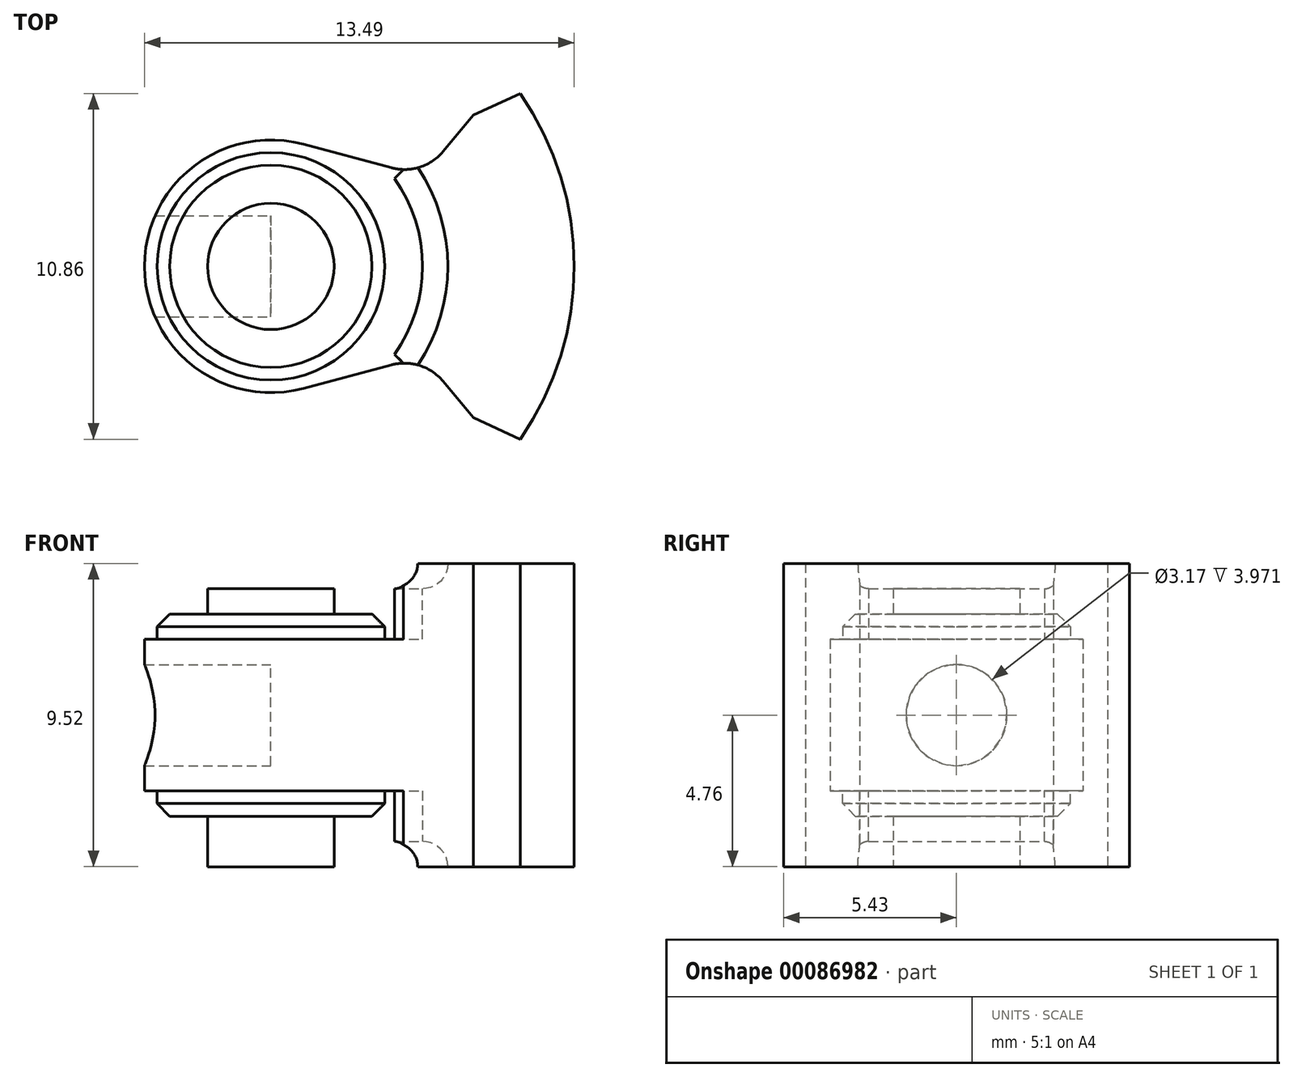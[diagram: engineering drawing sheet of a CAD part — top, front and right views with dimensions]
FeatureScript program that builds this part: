
annotation { "Feature Type Name" : "Feature", "Feature Type Description" : "" }
export const myFeature = defineFeature(function(context is Context, id is Id, definition is map)
    precondition{}
    {
        {
            var Q0;
            Q0=qCreatedBy(makeId("Top.planeOp"),FACE);
            var sketch = newSketch(context, id + "F0", { "sketchPlane" : qUnion([Q0])});
            skCircle(sketch, "E0", {"center": v(0, 0) * mm, "radius": 9.53 * mm, "construction": true});
            skCircle(sketch, "E1", {"center": v(0, 0) * mm, "radius": 7.94 * mm, "construction": true});
            skCircle(sketch, "E2", {"center": v(0, 0) * mm, "radius": 4.76 * mm, "construction": true});
            skCircle(sketch, "E3", {"center": v(0, 0) * mm, "radius": 3.97 * mm, "construction": true});
            skLineSegment(sketch, "E4", {"start": v(0, 0) * mm, "end": v(2.38, 0) * mm, "construction": true});
            skLineSegment(sketch, "E5", {"start": v(2.38, 0) * mm, "end": v(11.06, 10.34) * mm, "construction": true});
            skLineSegment(sketch, "E6", {"start": v(2.38, 0) * mm, "end": v(10.97, -10.23) * mm, "construction": true});
            skLineSegment(sketch, "E7", {"start": v(6.36, 4.75) * mm, "end": v(7.83, 5.43) * mm});
            skLineSegment(sketch, "E8", {"start": v(6.36, -4.75) * mm, "end": v(7.83, -5.43) * mm});
            skLineSegment(sketch, "E9", {"start": v(1.03, -3.83) * mm, "end": v(6.07, -2.48) * mm, "construction": true});
            skLineSegment(sketch, "E10", {"start": v(1.03, 3.83) * mm, "end": v(5.56, 2.62) * mm, "construction": true});
            skArc(sketch, "E11", {"start": v(5.4, -3.6) * mm, "mid": v(4.67, -3.11) * mm, "end": v(3.78, -3.1) * mm});
            skArc(sketch, "E12", {"start": v(3.78, 3.1) * mm, "mid": v(4.67, 3.11) * mm, "end": v(5.4, 3.6) * mm});
            skArc(sketch, "E13", {"start": v(1.03, 3.83) * mm, "mid": v(-2.42, 3.15) * mm, "end": v(-3.97, 0) * mm});
            skLineSegment(sketch, "E14", {"start": v(5.4, 3.6) * mm, "end": v(6.36, 4.75) * mm});
            skLineSegment(sketch, "E15", {"start": v(1.03, 3.83) * mm, "end": v(3.78, 3.1) * mm});
            skLineSegment(sketch, "E16", {"start": v(1.03, -3.83) * mm, "end": v(3.78, -3.1) * mm});
            skLineSegment(sketch, "E17", {"start": v(6.36, -4.75) * mm, "end": v(5.4, -3.6) * mm});
            skArc(sketch, "E18", {"start": v(9.52, 0) * mm, "mid": v(9.1, 2.84) * mm, "end": v(7.83, 5.43) * mm});
            skLineSegment(sketch, "E19", {"start": v(-3.97, 0) * mm, "end": v(9.53, 0) * mm});
            skSolve(sketch);
        }
        {
            var Q0;
            Q0=makeQuery(id+"F0.imprint","IMPRINT",FACE,{"disambiguationData":[TD([[makeQuery(id+"F0.imprint","IMPRINT",EDGE,{"derivedFrom":sQuery(id+"F0.wireOp",EDGE,"E7")}),-1.0]])]});
            extrude(context, id + "F1", {"entities" : qUnion([Q0]), "depth" : 4.76 * mm});
        }
        {
            var Q0;
            Q0=makeQuery(id+"F1.opExtrude","CAP_FACE",FACE,{"disambiguationData":[OSD([sQuery(id+"F0.wireOp",EDGE,"E7"),sQuery(id+"F0.wireOp",EDGE,"E8"),sQuery(id+"F0.wireOp",EDGE,"E11"),sQuery(id+"F0.wireOp",EDGE,"E12"),sQuery(id+"F0.wireOp",EDGE,"E13"),sQuery(id+"F0.wireOp",EDGE,"E14"),sQuery(id+"F0.wireOp",EDGE,"E15"),sQuery(id+"F0.wireOp",EDGE,"E16"),sQuery(id+"F0.wireOp",EDGE,"E17"),sQuery(id+"F0.wireOp",EDGE,"E18")])],"isStart":false});
            var sketch = newSketch(context, id + "F2", { "sketchPlane" : qUnion([Q0])});
            skCircle(sketch, "E20", {"center": v(0, 0) * mm, "radius": 4.76 * mm, "construction": true});
            skCircle(sketch, "E21", {"center": v(0, 0) * mm, "radius": 3.97 * mm, "construction": true});
            skLineSegment(sketch, "E22", {"start": v(1.03, 3.83) * mm, "end": v(3.57, 3.15) * mm});
            skLineSegment(sketch, "E23", {"start": v(1.03, -3.83) * mm, "end": v(3.57, -3.15) * mm});
            skArc(sketch, "E24", {"start": v(3.57, -3.15) * mm, "mid": v(4.76, 0) * mm, "end": v(3.57, 3.15) * mm});
            skArc(sketch, "E25", {"start": v(1.03, 3.83) * mm, "mid": v(-3.97, 0) * mm, "end": v(1.03, -3.83) * mm, "construction": true});
            skSolve(sketch);
        }
        {
            var Q0;
            Q0=makeQuery(id+"F2.imprint","IMPRINT",FACE,{"disambiguationData":[TD([[makeQuery(id+"F2.imprint","IMPRINT",EDGE,{"derivedFrom":sQuery(id+"F2.wireOp",EDGE,"E22")}),-1.0]])]});
            extrude(context, id + "F3", {"entities" : qUnion([Q0]), "operationType" : NewBodyOperationType.REMOVE, "oppositeDirection" : true, "depth" : 2.38 * mm});
        }
        {
            var Q0;
            Q0=qCreatedBy(makeId("Front.planeOp"),FACE);
            var sketch = newSketch(context, id + "F4", { "sketchPlane" : qUnion([Q0])});
            skLineSegment(sketch, "E26", {"start": v(0, 0) * mm, "end": v(0, 4.76) * mm, "construction": true});
            skLineSegment(sketch, "E27", {"start": v(0, 4.76) * mm, "end": v(4.76, 4.76) * mm, "construction": true});
            skCircle(sketch, "E28", {"center": v(4.76, 4.76) * mm, "radius": 0.8 * mm});
            skSolve(sketch);
        }
        {
            var Q0;
            Q0=makeQuery(id+"F1.opExtrude","CAP_FACE",FACE,{"disambiguationData":[OSD([sQuery(id+"F0.wireOp",EDGE,"E7"),sQuery(id+"F0.wireOp",EDGE,"E8"),sQuery(id+"F0.wireOp",EDGE,"E11"),sQuery(id+"F0.wireOp",EDGE,"E12"),sQuery(id+"F0.wireOp",EDGE,"E13"),sQuery(id+"F0.wireOp",EDGE,"E14"),sQuery(id+"F0.wireOp",EDGE,"E15"),sQuery(id+"F0.wireOp",EDGE,"E16"),sQuery(id+"F0.wireOp",EDGE,"E17"),sQuery(id+"F0.wireOp",EDGE,"E18")])],"isStart":false});
            var sketch = newSketch(context, id + "F5", { "sketchPlane" : qUnion([Q0])});
            skArc(sketch, "E29", {"start": v(4.76, 0) * mm, "mid": v(4.45, 1.69) * mm, "end": v(3.57, 3.15) * mm});
            skSolve(sketch);
        }
        {
            var Q0;
            Q0 = qSketchRegion(id + "F4", true);
            var Q1;
            Q1=sQuery(id+"F4.wireOp",EDGE,"E28");
            var Q2;
            Q2=sQuery(id+"F5.wireOp",EDGE,"E29");
            sweep(context, id + "F6", {"operationType" : NewBodyOperationType.REMOVE, "profiles" : qUnion([Q0]), "surfaceProfiles" : qUnion([Q1]), "path" : qUnion([Q2])});
        }
        {
            var Q0;
            Q0=makeQuery(id+"F3.boolean.opBoolean","COPY",FACE,{"derivedFrom":makeQuery(id+"F3.opExtrude","CAP_FACE",FACE,{"disambiguationData":[OSD([sQuery(id+"F0.wireOp",EDGE,"E13"),sQuery(id+"F0.wireOp",EDGE,"E19"),sQuery(id+"F2.wireOp",EDGE,"E22"),sQuery(id+"F2.wireOp",EDGE,"E24")])],"isStart":false})});
            var sketch = newSketch(context, id + "F7", { "sketchPlane" : qUnion([Q0])});
            skCircle(sketch, "E30", {"center": v(0, 0) * mm, "radius": 4.76 * mm, "construction": true});
            skLineSegment(sketch, "E31", {"start": v(3.88, 2.76) * mm, "end": v(4.16, 3.04) * mm});
            skLineSegment(sketch, "E32", {"start": v(4.16, 3.04) * mm, "end": v(2.58, 3.04) * mm, "construction": true});
            skLineSegment(sketch, "E33", {"start": v(3.88, 2.76) * mm, "end": v(2.69, 3.57) * mm});
            skLineSegment(sketch, "E34", {"start": v(2.69, 3.57) * mm, "end": v(4.16, 3.67) * mm});
            skLineSegment(sketch, "E35", {"start": v(4.16, 3.67) * mm, "end": v(4.16, 3.04) * mm});
            skSolve(sketch);
        }
        {
            var Q0;
            {var subQ4=sQuery(id+"F7.wireOp",EDGE,"E31");Q0=makeQuery(id+"F7.imprint","IMPRINT",FACE,{"disambiguationData":[TD([[makeQuery(id+"F7.imprint","IMPRINT",EDGE,{"derivedFrom":subQ4}),1.0]])]});}
            extrude(context, id + "F8", {"entities" : qUnion([Q0]), "operationType" : NewBodyOperationType.REMOVE, "depth" : 25.4 * mm});
        }
        {
            var Q0;
            Q0=makeQuery(id+"F1.opExtrude","SWEPT_BODY",BODY,{"disambiguationData":[OSD([sQuery(id+"F0.wireOp",EDGE,"E7"),sQuery(id+"F0.wireOp",EDGE,"E12"),sQuery(id+"F0.wireOp",EDGE,"E13"),sQuery(id+"F0.wireOp",EDGE,"E14"),sQuery(id+"F0.wireOp",EDGE,"E15"),sQuery(id+"F0.wireOp",EDGE,"E18"),sQuery(id+"F0.wireOp",EDGE,"E19")])]});
            var Q1;
            Q1=makeQuery(id+"F1.opExtrude","SWEPT_FACE",FACE,{"disambiguationData":[OSD([sQuery(id+"F0.wireOp",EDGE,"E19")])]});
            mirror(context, id + "F9", {"operationType" : NewBodyOperationType.ADD, "entities" : qUnion([Q0]), "mirrorPlane" : qUnion([Q1])});
        }
        {
            var Q0;
            Q0=qCreatedBy(makeId("Top.planeOp"),FACE);
            var sketch = newSketch(context, id + "F10", { "sketchPlane" : qUnion([Q0])});
            skCircle(sketch, "E36", {"center": v(0, 0) * mm, "radius": 3.57 * mm});
            skSolve(sketch);
        }
        {
            var Q0;
            Q0 = qSketchRegion(id + "F10", true);
            extrude(context, id + "F11", {"entities" : qUnion([Q0]), "operationType" : NewBodyOperationType.ADD, "depth" : 3.17 * mm});
        }
        {
            var Q0;
            Q0=qCreatedBy(makeId("Top.planeOp"),FACE);
            var sketch = newSketch(context, id + "F12", { "sketchPlane" : qUnion([Q0])});
            skCircle(sketch, "E37", {"center": v(0, 0) * mm, "radius": 1.98 * mm});
            skSolve(sketch);
        }
        {
            var Q0;
            Q0=makeQuery(id+"F11.opExtrude","CAP_EDGE",EDGE,{"disambiguationData":[OSD([sQuery(id+"F10.wireOp",EDGE,"E36")])],"isStart":false});
            chamfer(context, id + "F13", {"entities" : qUnion([Q0]), "chamferType" : ChamferType.OFFSET_ANGLE, "width" : 0.4 * mm, "oppositeDirection" : false, "angle" : 45 * degree, "tangentPropagation" : true});
        }
        {
            var Q0;
            Q0=makeQuery(id+"F1.opExtrude","SWEPT_BODY",BODY,{"disambiguationData":[OSD([sQuery(id+"F0.wireOp",EDGE,"E7"),sQuery(id+"F0.wireOp",EDGE,"E12"),sQuery(id+"F0.wireOp",EDGE,"E13"),sQuery(id+"F0.wireOp",EDGE,"E14"),sQuery(id+"F0.wireOp",EDGE,"E15"),sQuery(id+"F0.wireOp",EDGE,"E18"),sQuery(id+"F0.wireOp",EDGE,"E19")])]});
            var Q1;
            Q1=qCreatedBy(makeId("Top.planeOp"),FACE);
            mirror(context, id + "F14", {"operationType" : NewBodyOperationType.ADD, "entities" : qUnion([Q0]), "mirrorPlane" : qUnion([Q1])});
        }
        {
            var Q0;
            Q0 = qSketchRegion(id + "F12", true);
            extrude(context, id + "F15", {"entities" : qUnion([Q0]), "operationType" : NewBodyOperationType.ADD, "depth" : 3.97 * mm, "hasSecondDirection" : true, "secondDirectionOppositeDirection" : true, "secondDirectionDepth" : 4.76 * mm});
        }
        {
            var Q0;
            Q0=qCreatedBy(makeId("Right.planeOp"),FACE);
            var sketch = newSketch(context, id + "F16", { "sketchPlane" : qUnion([Q0])});
            skCircle(sketch, "E38", {"center": v(0, 0) * mm, "radius": 1.59 * mm});
            skSolve(sketch);
        }
        {
            var Q0;
            Q0 = qSketchRegion(id + "F16", true);
            extrude(context, id + "F17", {"entities" : qUnion([Q0]), "operationType" : NewBodyOperationType.REMOVE, "oppositeDirection" : true, "depth" : 25.4 * mm});
        }
    });
